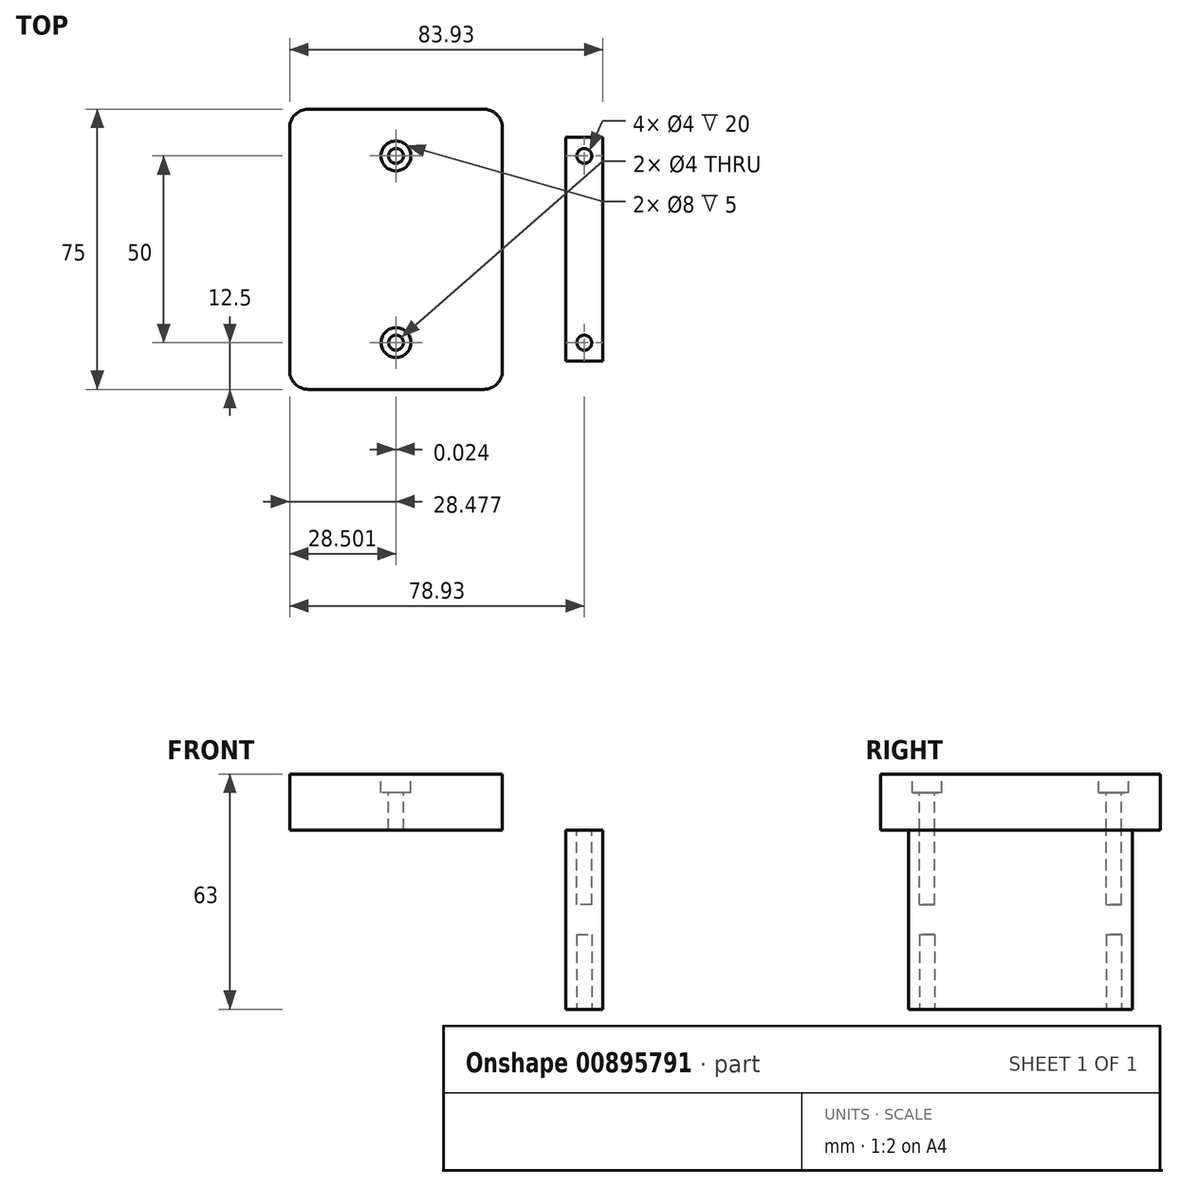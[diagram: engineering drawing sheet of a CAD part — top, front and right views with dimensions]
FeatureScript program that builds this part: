
annotation { "Feature Type Name" : "Feature", "Feature Type Description" : "" }
export const myFeature = defineFeature(function(context is Context, id is Id, definition is map)
    precondition{}
    {
        {
            var Q0;
            Q0=qCreatedBy(makeId("Front.planeOp"),FACE);
            var sketch = newSketch(context, id + "F0", { "sketchPlane" : qUnion([Q0])});
            skLineSegment(sketch, "E0.bottom", {"start": v(0, 0) * mm, "end": v(10, 0) * mm});
            skLineSegment(sketch, "E0.top", {"start": v(0, 48) * mm, "end": v(10, 48) * mm});
            skLineSegment(sketch, "E0.left", {"start": v(0, 0) * mm, "end": v(0, 48) * mm});
            skLineSegment(sketch, "E0.right", {"start": v(10, 0) * mm, "end": v(10, 48) * mm});
            skSolve(sketch);
        }
        {
            var Q0;
            Q0 = qSketchRegion(id + "F0", true);
            extrude(context, id + "F1", {"entities" : qUnion([Q0]), "depth" : 60 * mm, "offsetDistance" : 25 * mm});
        }
        {
            var Q0;
            Q0=makeQuery(id+"F1.opExtrude","SWEPT_FACE",FACE,{"disambiguationData":[OSD([sQuery(id+"F0.wireOp",EDGE,"E0.bottom")])]});
            var sketch = newSketch(context, id + "F2", { "sketchPlane" : qUnion([Q0])});
            skCircle(sketch, "E1", {"center": v(5, 55) * mm, "radius": 2 * mm});
            skCircle(sketch, "E2", {"center": v(5, 5) * mm, "radius": 2 * mm});
            skSolve(sketch);
        }
        {
            var Q0;
            Q0 = qSketchRegion(id + "F2", true);
            extrude(context, id + "F3", {"entities" : qUnion([Q0]), "operationType" : NewBodyOperationType.REMOVE, "oppositeDirection" : true, "depth" : 20 * mm, "offsetDistance" : 25 * mm});
        }
        {
            var Q0;
            Q0=makeQuery(id+"F1.opExtrude","SWEPT_FACE",FACE,{"disambiguationData":[OSD([sQuery(id+"F0.wireOp",EDGE,"E0.top")])]});
            var sketch = newSketch(context, id + "F4", { "sketchPlane" : qUnion([Q0])});
            skCircle(sketch, "E3", {"center": v(5, -5) * mm, "radius": 2 * mm});
            skCircle(sketch, "E4", {"center": v(5, -55) * mm, "radius": 2 * mm});
            skLineSegment(sketch, "E5.top", {"start": v(-68.93, -67.5) * mm, "end": v(-21.93, -67.5) * mm});
            skLineSegment(sketch, "E5.left", {"start": v(-73.93, 2.5) * mm, "end": v(-73.93, -62.5) * mm});
            skLineSegment(sketch, "E5.right", {"start": v(-16.93, 2.5) * mm, "end": v(-16.93, -62.5) * mm});
            skPoint(sketch, "E6.visualSharp", {"position": v(-73.93, 0) * mm});
            skArc(sketch, "E6.filletArc", {"start": v(-68.95, 7.5) * mm, "mid": v(-72.47, 6.03) * mm, "end": v(-73.93, 2.5) * mm});
            skPoint(sketch, "E7.visualSharp", {"position": v(-16.93, 0) * mm});
            skArc(sketch, "E7.filletArc", {"start": v(-16.93, 2.5) * mm, "mid": v(-18.4, 6.04) * mm, "end": v(-21.95, 7.5) * mm});
            skPoint(sketch, "E8.visualSharp", {"position": v(-16.93, -67.5) * mm});
            skArc(sketch, "E8.filletArc", {"start": v(-21.93, -67.5) * mm, "mid": v(-18.4, -66.04) * mm, "end": v(-16.93, -62.5) * mm});
            skPoint(sketch, "E9.visualSharp", {"position": v(-73.93, -67.5) * mm});
            skArc(sketch, "E9.filletArc", {"start": v(-73.93, -62.5) * mm, "mid": v(-72.46, -66.04) * mm, "end": v(-68.93, -67.5) * mm});
            skLineSegment(sketch, "E10", {"start": v(-21.95, 7.5) * mm, "end": v(-68.95, 7.5) * mm});
            skLineSegment(sketch, "E11", {"start": v(-45.45, -30) * mm, "end": v(-13.57, -30) * mm});
            skSolve(sketch);
        }
        {
            var Q0;
            Q0 = qSketchRegion(id + "F4", true);
            extrude(context, id + "F5", {"entities" : qUnion([Q0]), "operationType" : NewBodyOperationType.REMOVE, "oppositeDirection" : true, "depth" : 20 * mm, "offsetDistance" : 25 * mm});
        }
        {
            var Q0;
            Q0=makeQuery(id+"F4.imprint","IMPRINT",FACE,{"disambiguationData":[TD([[makeQuery(id+"F4.imprint","IMPRINT",EDGE,{"derivedFrom":sQuery(id+"F4.wireOp",EDGE,"E5.top")}),1.0]])]});
            extrude(context, id + "F6", {"entities" : qUnion([Q0]), "depth" : 15 * mm, "offsetDistance" : 25 * mm});
        }
        {
            var Q0;
            Q0=makeQuery(id+"F6.opExtrude","CAP_FACE",FACE,{"disambiguationData":[OSD([sQuery(id+"F4.wireOp",EDGE,"E5.top"),sQuery(id+"F4.wireOp",EDGE,"E5.left"),sQuery(id+"F4.wireOp",EDGE,"E5.right"),sQuery(id+"F4.wireOp",EDGE,"E6.filletArc"),sQuery(id+"F4.wireOp",EDGE,"E7.filletArc"),sQuery(id+"F4.wireOp",EDGE,"E8.filletArc"),sQuery(id+"F4.wireOp",EDGE,"E9.filletArc"),sQuery(id+"F4.wireOp",EDGE,"E10")])],"isStart":false});
            var sketch = newSketch(context, id + "F7", { "sketchPlane" : qUnion([Q0])});
            skCircle(sketch, "E12", {"center": v(-45.43, -55) * mm, "radius": 2 * mm});
            skCircle(sketch, "E13", {"center": v(-45.43, -5) * mm, "radius": 2 * mm});
            skCircle(sketch, "E14", {"center": v(-45.45, -5) * mm, "radius": 4 * mm});
            skCircle(sketch, "E15", {"center": v(-45.43, -55) * mm, "radius": 4 * mm});
            skSolve(sketch);
        }
        {
            var Q0;
            Q0=makeQuery(id+"F7.imprint","IMPRINT",FACE,{"disambiguationData":[TD([[makeQuery(id+"F7.imprint","IMPRINT",EDGE,{"derivedFrom":sQuery(id+"F7.wireOp",EDGE,"E12")}),1.0]])]});
            var Q1;
            Q1=makeQuery(id+"F7.imprint","IMPRINT",FACE,{"disambiguationData":[TD([[makeQuery(id+"F7.imprint","IMPRINT",EDGE,{"derivedFrom":sQuery(id+"F7.wireOp",EDGE,"E13")}),1.0]])]});
            extrude(context, id + "F8", {"entities" : qUnion([Q0, Q1]), "operationType" : NewBodyOperationType.REMOVE, "endBound" : BoundingType.THROUGH_ALL, "oppositeDirection" : true, "depth" : 5 * mm, "offsetDistance" : 25 * mm});
        }
        {
            var Q0;
            Q0 = qSketchRegion(id + "F7", true);
            extrude(context, id + "F9", {"entities" : qUnion([Q0]), "operationType" : NewBodyOperationType.REMOVE, "oppositeDirection" : true, "depth" : 5 * mm, "offsetDistance" : 25 * mm});
        }
    });
